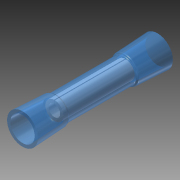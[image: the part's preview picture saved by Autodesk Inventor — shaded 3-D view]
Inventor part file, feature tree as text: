
AUTODESK INVENTOR PART (.ipt)
format: ipt  version: 2014 (Build 180170000, 170)  size: 177,152 bytes
history: native  units: in
note: dims shown in document units (in); Inventor stores cm internally (conversion verified against a paired STEP export)
features: sketch x4, extrude x3, projected_geometry x3, fillet x1, mirror x1, shell x1, revolve x1
ambient origin geometry x8: Origin, YZ Plane, XZ Plane, XY Plane, X Axis, Y Axis, Z Axis, Center Point
bodies: Solid1 (feature_tree), Solid2 (feature_tree)
feature tree (14):
  extrude  "Extrusion1"  Depth=0.65in TaperAngle=0.0deg
  extrude  "Extrusion2"  Depth=0.02in
  fillet  "Fillet1"  Radius=0.02in
  mirror  "Mirror1"
  shell  "Shell1"  Thickness=0.03in
  revolve  "Revolution1"  Angle=90.0deg
  extrude  "Extrusion3"  [1 undecoded]
  sketch  "Sketch1"  dims[d0=0.23in d1=0.65in d2=0.0in]
  sketch  "Sketch2"  dims[d3=0.256in d4=0.306in d5=0.0206in d6=0.02in d7=0.03in]
  projected_geometry  "Projected Loop1"
  sketch  "Sketch3"  dims[d8=0.0315in d9=90.0deg]
  sketch  "Sketch4"  dims[d10=0.306in d11=0.0in]
  projected_geometry  "Projected Loop2"
  projected_geometry  "Project Cut Edges1"
note: 1 required parameter value undecoded (feature->parameter linkage not recoverable at this tier; creation-order binding heuristic only, values carry confidence <= 0.55)
